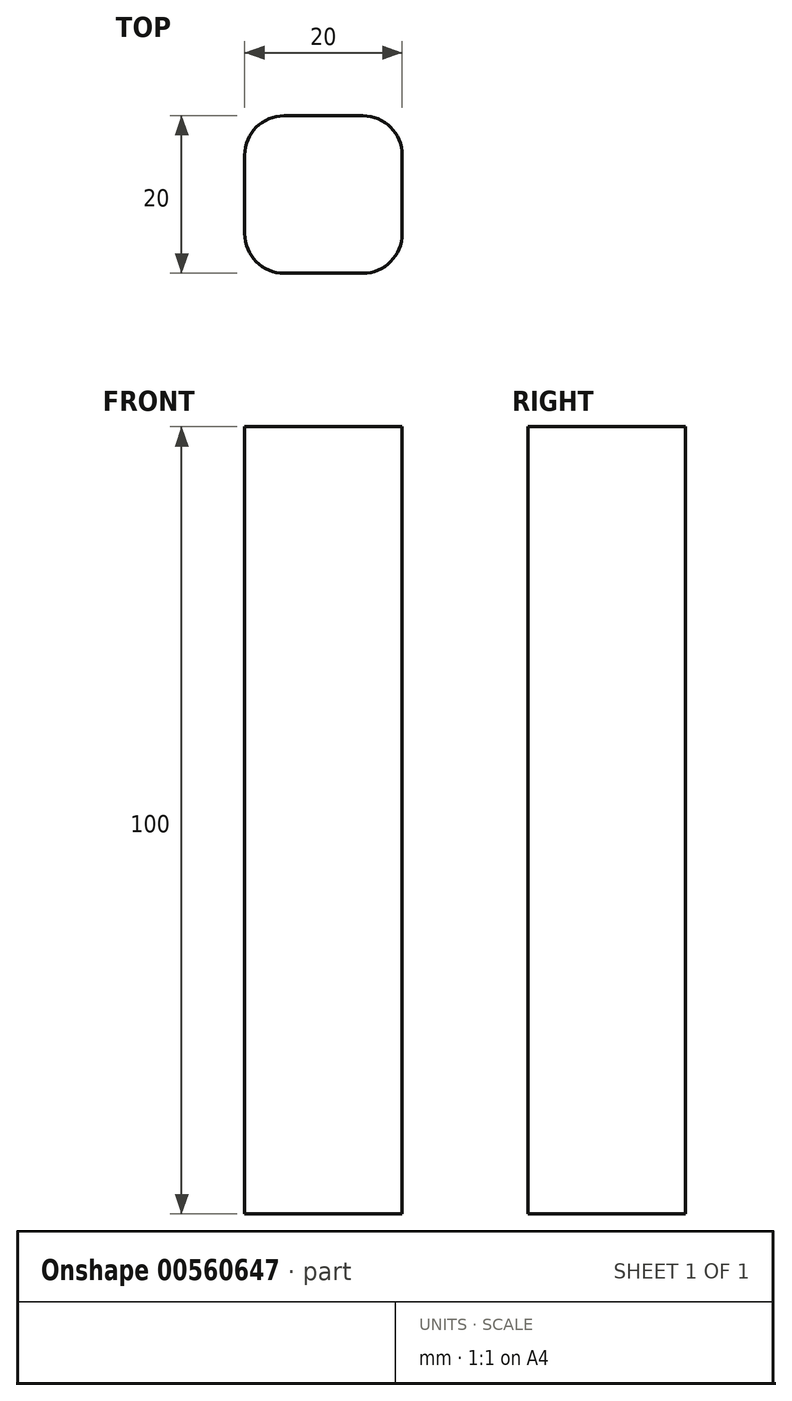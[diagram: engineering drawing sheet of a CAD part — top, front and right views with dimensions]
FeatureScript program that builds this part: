
annotation { "Feature Type Name" : "Feature", "Feature Type Description" : "" }
export const myFeature = defineFeature(function(context is Context, id is Id, definition is map)
    precondition{}
    {
        {
            var Q0;
            Q0=qCreatedBy(makeId("Top.planeOp"),FACE);
            var sketch = newSketch(context, id + "F0", { "sketchPlane" : qUnion([Q0])});
            skLineSegment(sketch, "E0", {"start": v(-34.12, 9.3) * mm, "end": v(-34.12, -0.7) * mm});
            skLineSegment(sketch, "E1", {"start": v(-29.12, -5.7) * mm, "end": v(-19.12, -5.7) * mm});
            skLineSegment(sketch, "E2", {"start": v(-14.12, -0.7) * mm, "end": v(-14.12, 9.3) * mm});
            skLineSegment(sketch, "E3", {"start": v(-19.12, 14.3) * mm, "end": v(-29.12, 14.3) * mm});
            skPoint(sketch, "E4.visualSharp", {"position": v(-34.12, 14.3) * mm});
            skArc(sketch, "E4.filletArc", {"start": v(-29.12, 14.3) * mm, "mid": v(-32.66, 12.83) * mm, "end": v(-34.12, 9.3) * mm});
            skPoint(sketch, "E5.visualSharp", {"position": v(-14.12, 14.3) * mm});
            skArc(sketch, "E5.filletArc", {"start": v(-14.12, 9.3) * mm, "mid": v(-15.59, 12.83) * mm, "end": v(-19.12, 14.3) * mm});
            skPoint(sketch, "E6.visualSharp", {"position": v(-14.12, -5.7) * mm});
            skArc(sketch, "E6.filletArc", {"start": v(-19.12, -5.7) * mm, "mid": v(-15.59, -4.24) * mm, "end": v(-14.12, -0.7) * mm});
            skPoint(sketch, "E7.visualSharp", {"position": v(-34.12, -5.7) * mm});
            skArc(sketch, "E7.filletArc", {"start": v(-34.12, -0.7) * mm, "mid": v(-32.66, -4.24) * mm, "end": v(-29.12, -5.7) * mm});
            skSolve(sketch);
        }
        {
            var Q0;
            Q0 = qSketchRegion(id + "F0", true);
            extrude(context, id + "F1", {"entities" : qUnion([Q0]), "depth" : 100 * mm, "offsetDistance" : 25 * mm});
        }
    });
